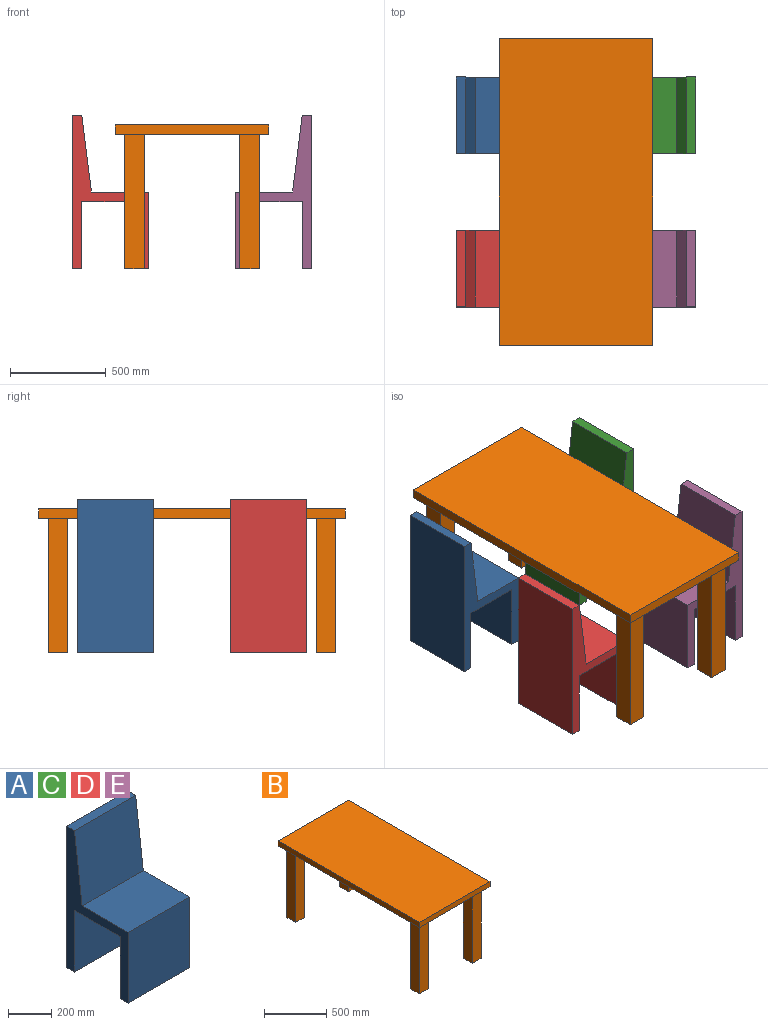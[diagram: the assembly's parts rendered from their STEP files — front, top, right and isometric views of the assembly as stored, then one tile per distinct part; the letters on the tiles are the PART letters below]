
ASSEMBLY  parts=5 mates=4
PART A: 12 faces, bbox 400x400x800 mm
  f0: plane 400x50mm, normal (0,0,-1), area 20000mm2, adj f1,f2,f5,f10
  f1: plane 800x400mm, normal (1,0,0), area 85000mm2, adj f0,f3,f4,f5,f6,f7,f8,f9
  f2: plane 800x400mm, normal (-1,0,0), area 85000mm2, adj f0,f3,f4,f5,f6,f7,f8,f9
  f3: plane 400x400mm, normal (0,-1,0), area 160000mm2, adj f1,f2,f4,f8
  f4: plane 400x50mm, normal (0,0,-1), area 20000mm2, adj f1,f2,f3,f9
  f5: plane 800x400mm, normal (0,1,0), area 320000mm2, adj f0,f1,f2,f6
  f6: plane 400x50mm, normal (0,0,1), area 20000mm2, adj f1,f2,f5,f7
  f7: plane 400x400mm, normal (0,-0.99,0.12), area 161245.2mm2, adj f1,f2,f6,f8
  f8: plane 400x300mm, normal (0,0,1), area 120000mm2, adj f1,f2,f3,f7
  f9: plane 400x350mm, normal (0,1,0), area 140000mm2, adj f1,f2,f4,f11
  f10: plane 400x350mm, normal (0,-1,0), area 140000mm2, adj f0,f1,f2,f11
  f11: plane 400x300mm, normal (0,0,-1), area 120000mm2, adj f1,f2,f9,f10
PART B: 26 faces, bbox 800x1600x750 mm
  f0: plane 800x50mm, normal (0,1,0), area 40000mm2, adj f1,f3,f4,f5
  f1: plane 1600x50mm, normal (-1,0,0), area 80000mm2, adj f0,f2,f4,f5
  f2: plane 800x50mm, normal (0,-1,0), area 40000mm2, adj f1,f3,f4,f5
  f3: plane 1600x50mm, normal (1,0,0), area 80000mm2, adj f0,f2,f4,f5
  f4: plane 1600x800mm, normal (0,0,1), area 1280000mm2, adj f0,f1,f2,f3
  f5: plane 1600x800mm, normal (0,0,-1), area 1240000mm2, adj f0,f1,f2,f3,f6,f7,f8,f9
  f6: plane 700x100mm, normal (0,-1,0), area 70000mm2, adj f5,f7,f9,f10
  f7: plane 700x100mm, normal (-1,0,0), area 70000mm2, adj f5,f6,f8,f10
  f8: plane 700x100mm, normal (0,1,0), area 70000mm2, adj f5,f7,f9,f10
  f9: plane 700x100mm, normal (1,0,0), area 70000mm2, adj f5,f6,f8,f10
  f10: plane 100x100mm, normal (0,0,-1), area 10000mm2, adj f6,f7,f8,f9
  f11: plane 700x100mm, normal (1,0,0), area 70000mm2, adj f5,f12,f14,f15
  f12: plane 700x100mm, normal (0,-1,0), area 70000mm2, adj f5,f11,f13,f15
  f13: plane 700x100mm, normal (-1,0,0), area 70000mm2, adj f5,f12,f14,f15
  f14: plane 700x100mm, normal (0,1,0), area 70000mm2, adj f5,f11,f13,f15
  f15: plane 100x100mm, normal (0,0,-1), area 10000mm2, adj f11,f12,f13,f14
  f16: plane 700x100mm, normal (1,0,0), area 70000mm2, adj f5,f17,f19,f20
  f17: plane 700x100mm, normal (0,-1,0), area 70000mm2, adj f5,f16,f18,f20
  f18: plane 700x100mm, normal (-1,0,0), area 70000mm2, adj f5,f17,f19,f20
  f19: plane 700x100mm, normal (0,1,0), area 70000mm2, adj f5,f16,f18,f20
  f20: plane 100x100mm, normal (0,0,-1), area 10000mm2, adj f16,f17,f18,f19
  f21: plane 700x100mm, normal (1,0,0), area 70000mm2, adj f5,f22,f24,f25
  f22: plane 700x100mm, normal (0,-1,0), area 70000mm2, adj f5,f21,f23,f25
  f23: plane 700x100mm, normal (-1,0,0), area 70000mm2, adj f5,f22,f24,f25
  f24: plane 700x100mm, normal (0,1,0), area 70000mm2, adj f5,f21,f23,f25
  f25: plane 100x100mm, normal (0,0,-1), area 10000mm2, adj f21,f22,f23,f24
PART C: same geometry as A
PART D: same geometry as A
PART E: same geometry as A
PLACE A rot(axis=(0,0,1),90deg) t=(-925,900,0)mm
PLACE B t=(100,-100,700)mm
PLACE C rot(axis=(0,0,-1),90deg) t=(325,1300,0)mm
PLACE D rot(axis=(0,0,1),90deg) t=(-925,100,0)mm
PLACE E rot(axis=(0,0,-1),90deg) t=(325,500,0)mm
MATE fastened B.f15 <-> A.f4  axis (0,0,-1) through (-600,1400,0)mm
MATE fastened B.f10 <-> D.f4  axis (0,0,-1) through (-600,0,0)mm
MATE fastened B.f20 <-> E.f4  axis (0,0,-1) through (0,0,0)mm
MATE fastened B.f25 <-> C.f4  axis (0,0,-1) through (0,1400,0)mm
